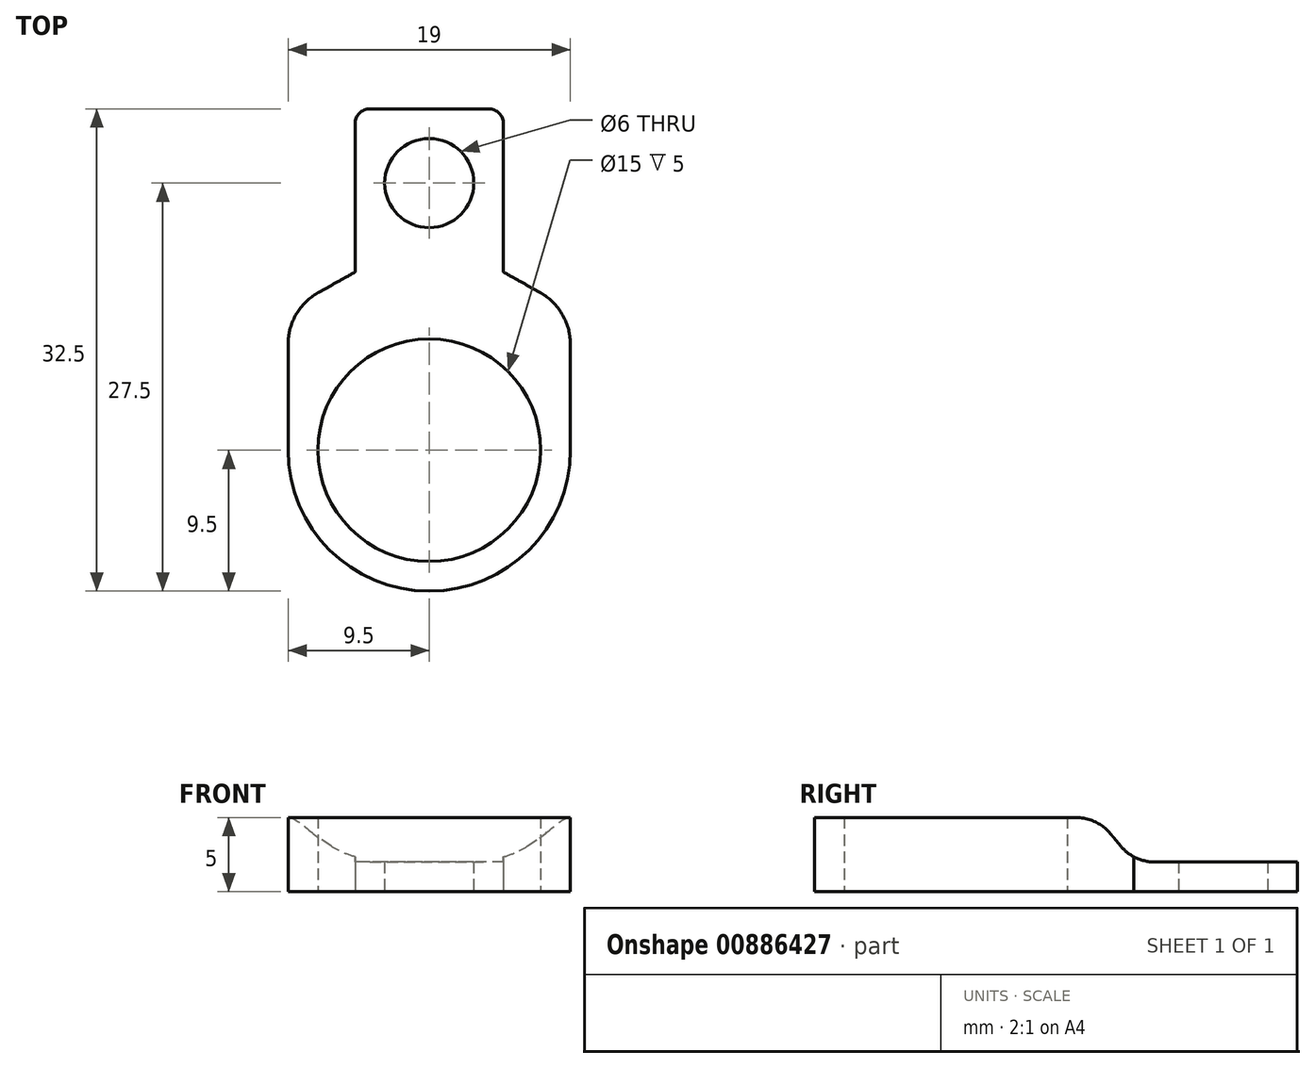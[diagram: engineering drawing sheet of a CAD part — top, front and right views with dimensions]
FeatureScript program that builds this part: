
annotation { "Feature Type Name" : "Feature", "Feature Type Description" : "" }
export const myFeature = defineFeature(function(context is Context, id is Id, definition is map)
    precondition{}
    {
        {
            var Q0;
            Q0=qCreatedBy(makeId("Top.planeOp"),FACE);
            var sketch = newSketch(context, id + "F0", { "sketchPlane" : qUnion([Q0])});
            skCircle(sketch, "E0", {"center": v(0, 0) * mm, "radius": 3 * mm});
            skCircle(sketch, "E1", {"center": v(0, 0) * mm, "radius": 5 * mm});
            skLineSegment(sketch, "E2", {"start": v(0, 0) * mm, "end": v(-5, 0) * mm, "construction": true});
            skLineSegment(sketch, "E3", {"start": v(0, 0) * mm, "end": v(5, 0) * mm, "construction": true});
            skLineSegment(sketch, "E4", {"start": v(0, 0) * mm, "end": v(0, 5) * mm, "construction": true});
            skLineSegment(sketch, "E5", {"start": v(5, 0) * mm, "end": v(5, 5) * mm});
            skLineSegment(sketch, "E6", {"start": v(5, 5) * mm, "end": v(0, 5) * mm});
            skLineSegment(sketch, "E7", {"start": v(-5, 0) * mm, "end": v(-5, 5) * mm});
            skLineSegment(sketch, "E8", {"start": v(-5, 5) * mm, "end": v(0, 5) * mm});
            skLineSegment(sketch, "E9", {"start": v(0, 0) * mm, "end": v(0, -5) * mm, "construction": true});
            skLineSegment(sketch, "E10", {"start": v(0, -5) * mm, "end": v(5, -5) * mm});
            skLineSegment(sketch, "E11", {"start": v(5, -5) * mm, "end": v(5, 0) * mm});
            skLineSegment(sketch, "E12", {"start": v(0, -5) * mm, "end": v(-5, -5) * mm});
            skLineSegment(sketch, "E13", {"start": v(-5, -5) * mm, "end": v(-5, 0) * mm});
            skLineSegment(sketch, "E14.bottom", {"start": v(-5, -5) * mm, "end": v(5, -5) * mm});
            skLineSegment(sketch, "E14.top", {"start": v(-5, -6) * mm, "end": v(5, -6) * mm});
            skLineSegment(sketch, "E14.left", {"start": v(-5, -5) * mm, "end": v(-5, -6) * mm});
            skLineSegment(sketch, "E14.right", {"start": v(5, -5) * mm, "end": v(5, -6) * mm});
            skSolve(sketch);
        }
        {
            var Q0;
            {var subQ2=sQuery(id+"F0.wireOp",EDGE,"E7");Q0=makeQuery(id+"F0.imprint","IMPRINT",FACE,{"disambiguationData":[TD([[makeQuery(id+"F0.imprint","IMPRINT",EDGE,{"derivedFrom":subQ2}),-1.0]])]});}
            var Q1;
            Q1=makeQuery(id+"F0.imprint","IMPRINT",FACE,{"disambiguationData":[TD([[makeQuery(id+"F0.imprint","IMPRINT",EDGE,{"derivedFrom":sQuery(id+"F0.wireOp",EDGE,"E0")}),-1.0]])]});
            var Q2;
            {var subQ0=sQuery(id+"F0.wireOp",EDGE,"E5");Q2=makeQuery(id+"F0.imprint","IMPRINT",FACE,{"disambiguationData":[TD([[makeQuery(id+"F0.imprint","IMPRINT",EDGE,{"derivedFrom":subQ0}),1.0]])]});}
            var Q3;
            {var subQ2=sQuery(id+"F0.wireOp",EDGE,"E10");Q3=makeQuery(id+"F0.imprint","IMPRINT",FACE,{"disambiguationData":[TD([[makeQuery(id+"F0.imprint","IMPRINT",EDGE,{"derivedFrom":subQ2}),1.0]])]});}
            var Q4;
            {var subQ2=sQuery(id+"F0.wireOp",EDGE,"E12");Q4=makeQuery(id+"F0.imprint","IMPRINT",FACE,{"disambiguationData":[TD([[makeQuery(id+"F0.imprint","IMPRINT",EDGE,{"derivedFrom":subQ2}),-1.0]])]});}
            var Q5;
            {var subQ0=sQuery(id+"F0.wireOp",EDGE,"E11");Q5=makeQuery(id+"F0.imprint","IMPRINT",FACE,{"disambiguationData":[TD([[makeQuery(id+"F0.imprint","IMPRINT",EDGE,{"derivedFrom":subQ0}),1.0]])]});}
            var Q6;
            {var subQ0=sQuery(id+"F0.wireOp",EDGE,"E13");Q6=makeQuery(id+"F0.imprint","IMPRINT",FACE,{"disambiguationData":[TD([[makeQuery(id+"F0.imprint","IMPRINT",EDGE,{"derivedFrom":subQ0}),-1.0]])]});}
            var Q7;
            Q7=makeQuery(id+"F0.imprint","IMPRINT",FACE,{"disambiguationData":[TD([[makeQuery(id+"F0.imprint","IMPRINT",EDGE,{"derivedFrom":sQuery(id+"F0.wireOp",EDGE,"E14.top")}),1.0]])]});
            extrude(context, id + "F1", {"entities" : qUnion([Q0, Q1, Q2, Q3, Q4, Q5, Q6, Q7]), "depth" : 2 * mm, "offsetDistance" : 25 * mm});
        }
        {
            var Q0;
            Q0=qCreatedBy(makeId("Top.planeOp"),FACE);
            cPlane(context, id + "F2", {"entities" : qUnion([Q0]), "cplaneType" : CPlaneType.OFFSET, "offset" : 4 * mm, "width" : 150 * mm, "height" : 150 * mm});
        }
        {
            var Q0;
            Q0=qCreatedBy(id+"F2.planeOp",FACE);
            var sketch = newSketch(context, id + "F3", { "sketchPlane" : qUnion([Q0])});
            skCircle(sketch, "E15.0", {"center": v(0, 0) * mm, "radius": 3 * mm});
            skLineSegment(sketch, "E16.0.0", {"start": v(-5, 5) * mm, "end": v(-5, 5) * mm});
            skCircle(sketch, "E17", {"center": v(0, -18) * mm, "radius": 7.5 * mm});
            skCircle(sketch, "E18.0", {"center": v(0, -18) * mm, "radius": 9.5 * mm});
            skLineSegment(sketch, "E19", {"start": v(-9.5, -18) * mm, "end": v(9.5, -18) * mm, "construction": true});
            skLineSegment(sketch, "E20", {"start": v(0, -18) * mm, "end": v(0, -8.5) * mm, "construction": true});
            skLineSegment(sketch, "E21", {"start": v(9.5, -18) * mm, "end": v(9.5, -8.5) * mm});
            skLineSegment(sketch, "E22", {"start": v(9.5, -8.5) * mm, "end": v(-9.5, -8.5) * mm});
            skLineSegment(sketch, "E23", {"start": v(-9.5, -8.5) * mm, "end": v(-9.5, -18) * mm});
            skSolve(sketch);
        }
        {
            var Q0;
            Q0=makeQuery(id+"F3.imprint","IMPRINT",FACE,{"disambiguationData":[TD([[makeQuery(id+"F3.imprint","IMPRINT",EDGE,{"derivedFrom":sQuery(id+"F3.wireOp",EDGE,"E17")}),-1.0]])]});
            var Q1;
            {var subQ0=sQuery(id+"F3.wireOp",EDGE,"E23");Q1=makeQuery(id+"F3.imprint","IMPRINT",FACE,{"disambiguationData":[TD([[makeQuery(id+"F3.imprint","IMPRINT",EDGE,{"derivedFrom":subQ0}),1.0]])]});}
            var Q2;
            {var subQ0=sQuery(id+"F3.wireOp",EDGE,"E21");Q2=makeQuery(id+"F3.imprint","IMPRINT",FACE,{"disambiguationData":[TD([[makeQuery(id+"F3.imprint","IMPRINT",EDGE,{"derivedFrom":subQ0}),1.0]])]});}
            extrude(context, id + "F4", {"entities" : qUnion([Q0, Q1, Q2]), "depth" : 1 * mm, "offsetDistance" : 25 * mm, "hasSecondDirection" : true, "secondDirectionOppositeDirection" : true, "secondDirectionDepth" : 4 * mm});
        }
        {
            var Q0;
            Q0=makeQuery(id+"F1.opExtrude","SWEPT_FACE",FACE,{"disambiguationData":[OSD([sQuery(id+"F0.wireOp",EDGE,"E14.top")])]});
            var Q1;
            Q1=makeQuery(id+"F4.opExtrude","SWEPT_FACE",FACE,{"disambiguationData":[OSD([sQuery(id+"F3.wireOp",EDGE,"E22")])]});
            loft(context, id + "F5", {"operationType" : NewBodyOperationType.ADD, "sheetProfilesArray" : [{ "sheetProfileEntities" : qUnion([Q0]) }, { "sheetProfileEntities" : qUnion([Q1]) }]});
        }
        {
            var Q0;
            {var subQ0=sQuery(id+"F3.wireOp",EDGE,"E23");var subQ1=sQuery(id+"F3.wireOp",EDGE,"E22");Q0=makeQuery(id+"F5.boolean.opBoolean","MERGE",EDGE,{"derivedFrom":[makeQuery(id+"F4.opExtrude","SWEPT_EDGE",EDGE,{"disambiguationData":[OSD([subQ1,subQ0])]}),makeQuery(id+"F5.opLoft","MID_CAP_EDGE",EDGE,{"disambiguationData":[OSD([subQ1,subQ0])],"capPos":1.0})]});}
            var Q1;
            {var subQ0=sQuery(id+"F3.wireOp",EDGE,"E22");var subQ1=sQuery(id+"F3.wireOp",EDGE,"E21");Q1=makeQuery(id+"F5.boolean.opBoolean","MERGE",EDGE,{"derivedFrom":[makeQuery(id+"F4.opExtrude","SWEPT_EDGE",EDGE,{"disambiguationData":[OSD([subQ1,subQ0])]}),makeQuery(id+"F5.opLoft","MID_CAP_EDGE",EDGE,{"disambiguationData":[OSD([subQ1,subQ0])],"capPos":1.0})]});}
            fillet(context, id + "F6", {"entities" : qUnion([Q0, Q1]), "radius" : 4 * mm, "tangentPropagation" : true, "allowEdgeOverflow" : false});
        }
        {
            var Q0;
            Q0=makeQuery(id+"F1.opExtrude","SWEPT_EDGE",EDGE,{"disambiguationData":[OSD([sQuery(id+"F0.wireOp",EDGE,"E7"),sQuery(id+"F0.wireOp",EDGE,"E8")])]});
            var Q1;
            Q1=makeQuery(id+"F1.opExtrude","SWEPT_EDGE",EDGE,{"disambiguationData":[OSD([sQuery(id+"F0.wireOp",EDGE,"E5"),sQuery(id+"F0.wireOp",EDGE,"E6")])]});
            fillet(context, id + "F7", {"entities" : qUnion([Q0, Q1]), "radius" : 1 * mm, "tangentPropagation" : true, "allowEdgeOverflow" : false});
        }
        {
            var Q0;
            {var subQ0=sQuery(id+"F3.wireOp",EDGE,"E22");var subQ1=makeQuery(id+"F4.opExtrude","CAP_EDGE",EDGE,{"disambiguationData":[OSD([subQ0])],"isStart":false});var subQ2=sQuery(id+"F3.wireOp",EDGE,"E23");var subQ3=sQuery(id+"F3.wireOp",EDGE,"E21");Q0=makeQuery(id+"F5.boolean.opBoolean","MERGE",EDGE,{"derivedFrom":[subQ1,makeQuery(id+"F5.opLoft","MID_CAP_EDGE",EDGE,{"disambiguationData":[OSD([subQ3,subQ0,subQ2]),TDD([makeQuery(id+"F4.opExtrude","CAP_VERTEX",VERTEX,{"disambiguationData":[OSD([subQ3,subQ0])],"isStart":false}),makeQuery(id+"F4.opExtrude","CAP_VERTEX",VERTEX,{"disambiguationData":[OSD([subQ0,subQ2])],"isStart":false}),subQ1])],"capPos":1.0})]});}
            var Q1;
            {var subQ0=sQuery(id+"F0.wireOp",EDGE,"E14.top");var subQ1=makeQuery(id+"F1.opExtrude","CAP_EDGE",EDGE,{"disambiguationData":[OSD([subQ0])],"isStart":false});var subQ2=sQuery(id+"F0.wireOp",EDGE,"E14.right");var subQ3=sQuery(id+"F0.wireOp",EDGE,"E14.left");Q1=makeQuery(id+"F5.boolean.opBoolean","MERGE",EDGE,{"derivedFrom":[subQ1,makeQuery(id+"F5.opLoft","MID_CAP_EDGE",EDGE,{"disambiguationData":[OSD([subQ0,subQ3,subQ2]),TDD([makeQuery(id+"F1.opExtrude","CAP_VERTEX",VERTEX,{"disambiguationData":[OSD([subQ0,subQ3])],"isStart":false}),makeQuery(id+"F1.opExtrude","CAP_VERTEX",VERTEX,{"disambiguationData":[OSD([subQ0,subQ2])],"isStart":false}),subQ1])],"capPos":0.0})]});}
            fillet(context, id + "F8", {"entities" : qUnion([Q0, Q1]), "tangentPropagation" : true, "radius" : 3 * mm, "defaultsChanged" : false, "vertexSettings" : [], "allowEdgeOverflow" : false});
        }
    });
